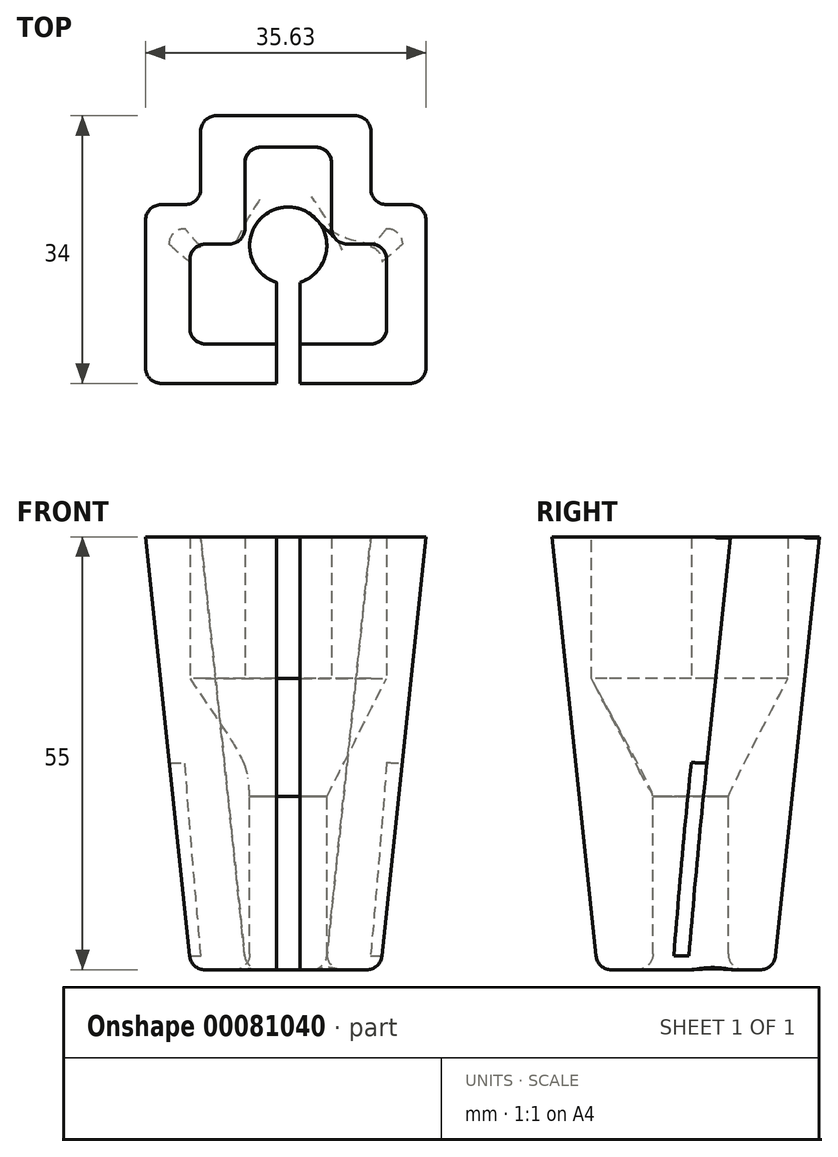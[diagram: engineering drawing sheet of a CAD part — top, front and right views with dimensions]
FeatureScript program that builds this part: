
annotation { "Feature Type Name" : "Feature", "Feature Type Description" : "" }
export const myFeature = defineFeature(function(context is Context, id is Id, definition is map)
    precondition{}
    {
        {
            var Q0;
            Q0=qCreatedBy(makeId("Top.planeOp"),FACE);
            var sketch = newSketch(context, id + "F0", { "sketchPlane" : qUnion([Q0])});
            skPoint(sketch, "E0.middle", {"position": v(0, 0) * mm});
            skLineSegment(sketch, "E1.bottom", {"start": v(10.5, -12.5) * mm, "end": v(-10.5, -12.5) * mm});
            skLineSegment(sketch, "E1.top", {"start": v(3.5, 12.5) * mm, "end": v(-3.5, 12.5) * mm});
            skLineSegment(sketch, "E1.left", {"start": v(12.5, -10.5) * mm, "end": v(12.5, -1.8) * mm});
            skLineSegment(sketch, "E1.right", {"start": v(-12.5, -10.5) * mm, "end": v(-12.5, -1.8) * mm});
            skLineSegment(sketch, "E2.top", {"start": v(-10.5, 0.2) * mm, "end": v(-7.5, 0.2) * mm});
            skLineSegment(sketch, "E2.right", {"start": v(-5.5, 10.5) * mm, "end": v(-5.5, 2.2) * mm});
            skLineSegment(sketch, "E3.top", {"start": v(10.5, 0.2) * mm, "end": v(7.5, 0.2) * mm});
            skLineSegment(sketch, "E3.right", {"start": v(5.5, 10.5) * mm, "end": v(5.5, 2.2) * mm});
            skPoint(sketch, "E4.newPointA", {"position": v(-5.5, 12.5) * mm});
            skPoint(sketch, "E4.newPointB", {"position": v(-12.5, 12.5) * mm});
            skArc(sketch, "E4.filletArc", {"start": v(-3.5, 12.5) * mm, "mid": v(-4.91, 11.91) * mm, "end": v(-5.5, 10.5) * mm});
            skArc(sketch, "E5.filletArc", {"start": v(5.5, 10.5) * mm, "mid": v(4.91, 11.91) * mm, "end": v(3.5, 12.5) * mm});
            skPoint(sketch, "E6.visualSharp", {"position": v(-5.5, 0.2) * mm});
            skArc(sketch, "E6.filletArc", {"start": v(-7.5, 0.2) * mm, "mid": v(-6.09, 0.79) * mm, "end": v(-5.5, 2.2) * mm});
            skPoint(sketch, "E7.visualSharp", {"position": v(5.5, 0.2) * mm});
            skArc(sketch, "E7.filletArc", {"start": v(5.5, 2.2) * mm, "mid": v(6.09, 0.79) * mm, "end": v(7.5, 0.2) * mm});
            skPoint(sketch, "E8.newPointA", {"position": v(-12.5, 0.2) * mm});
            skArc(sketch, "E8.filletArc", {"start": v(-10.5, 0.2) * mm, "mid": v(-11.91, -0.39) * mm, "end": v(-12.5, -1.8) * mm});
            skArc(sketch, "E9.filletArc", {"start": v(12.5, -1.8) * mm, "mid": v(11.91, -0.39) * mm, "end": v(10.5, 0.2) * mm});
            skArc(sketch, "E10.filletArc", {"start": v(15, 1.56) * mm, "mid": v(14.95, 1.99) * mm, "end": v(14.82, 2.4) * mm});
            skPoint(sketch, "E11.newPointA", {"position": v(-15, 2) * mm});
            skArc(sketch, "E11.filletArc", {"start": v(-14.82, 2.4) * mm, "mid": v(-14.95, 1.99) * mm, "end": v(-15, 1.56) * mm});
            skPoint(sketch, "E12.visualSharp", {"position": v(-12.5, -12.5) * mm});
            skArc(sketch, "E12.filletArc", {"start": v(-12.5, -10.5) * mm, "mid": v(-11.91, -11.91) * mm, "end": v(-10.5, -12.5) * mm});
            skPoint(sketch, "E13.visualSharp", {"position": v(12.5, -12.5) * mm});
            skArc(sketch, "E13.filletArc", {"start": v(10.5, -12.5) * mm, "mid": v(11.91, -11.91) * mm, "end": v(12.5, -10.5) * mm});
            skSolve(sketch);
        }
        {
            var Q0;
            Q0 = qSketchRegion(id + "F0", true);
            extrude(context, id + "F1", {"entities" : qUnion([Q0]), "depth" : 18 * mm});
        }
        {
            var Q0;
            Q0=makeQuery(id+"F1.opExtrude","CAP_FACE",FACE,{"disambiguationData":[OSD([sQuery(id+"F0.wireOp",EDGE,"E1.bottom"),sQuery(id+"F0.wireOp",EDGE,"E1.top"),sQuery(id+"F0.wireOp",EDGE,"E1.left"),sQuery(id+"F0.wireOp",EDGE,"E1.right"),sQuery(id+"F0.wireOp",EDGE,"E2.top"),sQuery(id+"F0.wireOp",EDGE,"E2.right"),sQuery(id+"F0.wireOp",EDGE,"E3.top"),sQuery(id+"F0.wireOp",EDGE,"E3.right"),sQuery(id+"F0.wireOp",EDGE,"E4.filletArc"),sQuery(id+"F0.wireOp",EDGE,"E5.filletArc"),sQuery(id+"F0.wireOp",EDGE,"E6.filletArc"),sQuery(id+"F0.wireOp",EDGE,"E7.filletArc"),sQuery(id+"F0.wireOp",EDGE,"E8.filletArc"),sQuery(id+"F0.wireOp",EDGE,"E9.filletArc"),sQuery(id+"F0.wireOp",EDGE,"E12.filletArc"),sQuery(id+"F0.wireOp",EDGE,"E13.filletArc")])],"isStart":true});
            cPlane(context, id + "F2", {"entities" : qUnion([Q0]), "cplaneType" : CPlaneType.OFFSET, "offset" : 15 * mm, "width" : 150 * mm, "height" : 150 * mm});
        }
        {
            var Q0;
            Q0=qCreatedBy(id+"F2.planeOp",FACE);
            var sketch = newSketch(context, id + "F3", { "sketchPlane" : qUnion([Q0])});
            skCircle(sketch, "E14", {"center": v(0, 0) * mm, "radius": 4.9 * mm});
            skSolve(sketch);
        }
        {
            var Q0;
            Q0 = qSketchRegion(id + "F3", true);
            extrude(context, id + "F4", {"entities" : qUnion([Q0]), "depth" : 30.48 * mm});
        }
        {
            var Q0;
            Q0=makeQuery(id+"F1.opExtrude","CAP_FACE",FACE,{"disambiguationData":[OSD([sQuery(id+"F0.wireOp",EDGE,"E1.bottom"),sQuery(id+"F0.wireOp",EDGE,"E1.top"),sQuery(id+"F0.wireOp",EDGE,"E1.left"),sQuery(id+"F0.wireOp",EDGE,"E1.right"),sQuery(id+"F0.wireOp",EDGE,"E2.top"),sQuery(id+"F0.wireOp",EDGE,"E2.right"),sQuery(id+"F0.wireOp",EDGE,"E3.top"),sQuery(id+"F0.wireOp",EDGE,"E3.right"),sQuery(id+"F0.wireOp",EDGE,"E4.filletArc"),sQuery(id+"F0.wireOp",EDGE,"E5.filletArc"),sQuery(id+"F0.wireOp",EDGE,"E6.filletArc"),sQuery(id+"F0.wireOp",EDGE,"E7.filletArc"),sQuery(id+"F0.wireOp",EDGE,"E8.filletArc"),sQuery(id+"F0.wireOp",EDGE,"E9.filletArc"),sQuery(id+"F0.wireOp",EDGE,"E12.filletArc"),sQuery(id+"F0.wireOp",EDGE,"E13.filletArc")])],"isStart":true});
            var Q1;
            Q1=makeQuery(id+"F4.opExtrude","CAP_FACE",FACE,{"disambiguationData":[OSD([sQuery(id+"F3.wireOp",EDGE,"E14")])],"isStart":true});
            loft(context, id + "F5", {"sheetProfilesArray" : [{ "sheetProfileEntities" : qUnion([Q0]) }, { "sheetProfileEntities" : qUnion([Q1]) }]});
        }
        {
            var Q0;
            Q0=makeQuery(id+"F1.opExtrude","CAP_FACE",FACE,{"disambiguationData":[OSD([sQuery(id+"F0.wireOp",EDGE,"E1.bottom"),sQuery(id+"F0.wireOp",EDGE,"E1.top"),sQuery(id+"F0.wireOp",EDGE,"E1.left"),sQuery(id+"F0.wireOp",EDGE,"E1.right"),sQuery(id+"F0.wireOp",EDGE,"E2.top"),sQuery(id+"F0.wireOp",EDGE,"E2.right"),sQuery(id+"F0.wireOp",EDGE,"E3.top"),sQuery(id+"F0.wireOp",EDGE,"E3.right"),sQuery(id+"F0.wireOp",EDGE,"E4.filletArc"),sQuery(id+"F0.wireOp",EDGE,"E5.filletArc"),sQuery(id+"F0.wireOp",EDGE,"E6.filletArc"),sQuery(id+"F0.wireOp",EDGE,"E7.filletArc"),sQuery(id+"F0.wireOp",EDGE,"E8.filletArc"),sQuery(id+"F0.wireOp",EDGE,"E9.filletArc"),sQuery(id+"F0.wireOp",EDGE,"E12.filletArc"),sQuery(id+"F0.wireOp",EDGE,"E13.filletArc")])],"isStart":false});
            var sketch = newSketch(context, id + "F6", { "sketchPlane" : qUnion([Q0])});
            skLineSegment(sketch, "E15.bottom", {"start": v(-9.13, 16.5) * mm, "end": v(8.5, 16.5) * mm});
            skLineSegment(sketch, "E15.top", {"start": v(-18.13, -17.5) * mm, "end": v(17.5, -17.5) * mm});
            skLineSegment(sketch, "E15.left", {"start": v(-18.13, 3.2) * mm, "end": v(-18.13, -17.5) * mm});
            skLineSegment(sketch, "E15.right", {"start": v(17.5, 3.2) * mm, "end": v(17.5, -17.5) * mm});
            skPoint(sketch, "E15.middle", {"position": v(0, -0.5) * mm});
            skLineSegment(sketch, "E16.bottom", {"start": v(17.5, 15.33) * mm, "end": v(10.5, 15.33) * mm});
            skLineSegment(sketch, "E16.top", {"start": v(15.5, 5.2) * mm, "end": v(12.5, 5.2) * mm});
            skLineSegment(sketch, "E16.left", {"start": v(17.5, 15.33) * mm, "end": v(17.5, 5.2) * mm});
            skLineSegment(sketch, "E16.right", {"start": v(10.5, 14.5) * mm, "end": v(10.5, 7.2) * mm});
            skLineSegment(sketch, "E17.bottom", {"start": v(-17.5, 15.33) * mm, "end": v(-10.5, 15.33) * mm});
            skLineSegment(sketch, "E17.top", {"start": v(-16.13, 5.2) * mm, "end": v(-13.13, 5.2) * mm});
            skLineSegment(sketch, "E17.left", {"start": v(-17.5, 15.33) * mm, "end": v(-17.5, 5.2) * mm});
            skLineSegment(sketch, "E17.right", {"start": v(-11.13, 14.5) * mm, "end": v(-11.13, 7.2) * mm});
            skPoint(sketch, "E18.visualSharp", {"position": v(10.5, 5.2) * mm});
            skArc(sketch, "E18.filletArc", {"start": v(10.5, 7.2) * mm, "mid": v(11.09, 5.79) * mm, "end": v(12.5, 5.2) * mm});
            skPoint(sketch, "E19.visualSharp", {"position": v(-11.13, 5.2) * mm});
            skArc(sketch, "E19.filletArc", {"start": v(-13.13, 5.2) * mm, "mid": v(-11.71, 5.79) * mm, "end": v(-11.13, 7.2) * mm});
            skPoint(sketch, "E20.newPointA", {"position": v(-17.5, 16.5) * mm});
            skArc(sketch, "E20.filletArc", {"start": v(-9.13, 16.5) * mm, "mid": v(-10.54, 15.91) * mm, "end": v(-11.13, 14.5) * mm});
            skPoint(sketch, "E21.newPointB", {"position": v(18.13, 16.5) * mm});
            skArc(sketch, "E21.filletArc", {"start": v(10.5, 14.5) * mm, "mid": v(9.91, 15.91) * mm, "end": v(8.5, 16.5) * mm});
            skArc(sketch, "E22.filletArc", {"start": v(17.5, 3.2) * mm, "mid": v(16.91, 4.61) * mm, "end": v(15.5, 5.2) * mm});
            skArc(sketch, "E23.filletArc", {"start": v(-16.13, 5.2) * mm, "mid": v(-17.54, 4.61) * mm, "end": v(-18.13, 3.2) * mm});
            skSolve(sketch);
        }
        {
            var Q0;
            Q0 = qSketchRegion(id + "F6", true);
            extrude(context, id + "F7", {"entities" : qUnion([Q0]), "oppositeDirection" : true, "depth" : 55 * mm, "hasDraft" : true, "draftAngle" : 6 * degree, "draftPullDirection" : true});
        }
        {
            var Q0;
            Q0=makeQuery(id+"F4.opExtrude","SWEPT_BODY",BODY,{"disambiguationData":[OSD([sQuery(id+"F3.wireOp",EDGE,"E14")])]});
            var Q1;
            Q1=makeQuery(id+"F1.opExtrude","SWEPT_BODY",BODY,{"disambiguationData":[OSD([sQuery(id+"F0.wireOp",EDGE,"E1.bottom"),sQuery(id+"F0.wireOp",EDGE,"E1.top"),sQuery(id+"F0.wireOp",EDGE,"E1.left"),sQuery(id+"F0.wireOp",EDGE,"E1.right"),sQuery(id+"F0.wireOp",EDGE,"E2.top"),sQuery(id+"F0.wireOp",EDGE,"E2.right"),sQuery(id+"F0.wireOp",EDGE,"E3.top"),sQuery(id+"F0.wireOp",EDGE,"E3.right"),sQuery(id+"F0.wireOp",EDGE,"E4.filletArc"),sQuery(id+"F0.wireOp",EDGE,"E5.filletArc"),sQuery(id+"F0.wireOp",EDGE,"E6.filletArc"),sQuery(id+"F0.wireOp",EDGE,"E7.filletArc"),sQuery(id+"F0.wireOp",EDGE,"E8.filletArc"),sQuery(id+"F0.wireOp",EDGE,"E9.filletArc"),sQuery(id+"F0.wireOp",EDGE,"E12.filletArc"),sQuery(id+"F0.wireOp",EDGE,"E13.filletArc")])]});
            var Q2;
            Q2=makeQuery(id+"F5.opLoft","SWEPT_BODY",BODY,{"disambiguationData":[OSD([sQuery(id+"F0.wireOp",EDGE,"E1.bottom"),sQuery(id+"F0.wireOp",EDGE,"E1.top"),sQuery(id+"F0.wireOp",EDGE,"E1.left"),sQuery(id+"F0.wireOp",EDGE,"E1.right"),sQuery(id+"F0.wireOp",EDGE,"E2.top"),sQuery(id+"F0.wireOp",EDGE,"E2.right"),sQuery(id+"F0.wireOp",EDGE,"E3.top"),sQuery(id+"F0.wireOp",EDGE,"E3.right"),sQuery(id+"F0.wireOp",EDGE,"E4.filletArc"),sQuery(id+"F0.wireOp",EDGE,"E5.filletArc"),sQuery(id+"F0.wireOp",EDGE,"E6.filletArc"),sQuery(id+"F0.wireOp",EDGE,"E7.filletArc"),sQuery(id+"F0.wireOp",EDGE,"E8.filletArc"),sQuery(id+"F0.wireOp",EDGE,"E9.filletArc"),sQuery(id+"F0.wireOp",EDGE,"E12.filletArc"),sQuery(id+"F0.wireOp",EDGE,"E13.filletArc"),sQuery(id+"F3.wireOp",EDGE,"E14")])]});
            var Q3;
            Q3=makeQuery(id+"F7.opExtrude","SWEPT_BODY",BODY,{"disambiguationData":[OSD([sQuery(id+"F6.wireOp",EDGE,"E15.bottom"),sQuery(id+"F6.wireOp",EDGE,"E15.top"),sQuery(id+"F6.wireOp",EDGE,"E15.left"),sQuery(id+"F6.wireOp",EDGE,"E15.right")])]});
            booleanBodies(context, id + "F8", {"operationType" : BooleanOperationType.SUBTRACTION, "tools" : qUnion([Q0, Q1, Q2]), "targets" : qUnion([Q3])});
        }
        {
            var Q0;
            Q0=makeQuery(id+"F7.opExtrude","CAP_FACE",FACE,{"disambiguationData":[OSD([sQuery(id+"F6.wireOp",EDGE,"E15.bottom"),sQuery(id+"F6.wireOp",EDGE,"E15.top"),sQuery(id+"F6.wireOp",EDGE,"E15.left"),sQuery(id+"F6.wireOp",EDGE,"E15.right")])],"isStart":false});
            var Q1;
            Q1=makeQuery(id+"F7.opExtrude","SWEPT_EDGE",EDGE,{"disambiguationData":[OSD([sQuery(id+"F6.wireOp",EDGE,"E15.top"),sQuery(id+"F6.wireOp",EDGE,"E15.right")])]});
            var Q2;
            Q2=makeQuery(id+"F7.opExtrude","SWEPT_EDGE",EDGE,{"disambiguationData":[OSD([sQuery(id+"F6.wireOp",EDGE,"E15.top"),sQuery(id+"F6.wireOp",EDGE,"E15.left")])]});
            var Q3;
            Q3=makeQuery(id+"F7.opExtrude","SWEPT_EDGE",EDGE,{"disambiguationData":[OSD([sQuery(id+"F6.wireOp",EDGE,"E15.bottom"),sQuery(id+"F6.wireOp",EDGE,"E15.left")])]});
            var Q4;
            Q4=makeQuery(id+"F7.opExtrude","SWEPT_EDGE",EDGE,{"disambiguationData":[OSD([sQuery(id+"F6.wireOp",EDGE,"E15.bottom"),sQuery(id+"F6.wireOp",EDGE,"E15.right")])]});
            fillet(context, id + "F9", {"entities" : qUnion([Q0, Q1, Q2, Q3, Q4]), "radius" : 2 * mm, "tangentPropagation" : true, "allowEdgeOverflow" : false});
        }
        {
            var Q0;
            Q0=qCreatedBy(makeId("Front.planeOp"),FACE);
            var sketch = newSketch(context, id + "F10", { "sketchPlane" : qUnion([Q0])});
            skLineSegment(sketch, "E24.bottom", {"start": v(1.5, 45) * mm, "end": v(-1.5, 45) * mm});
            skLineSegment(sketch, "E24.top", {"start": v(1.5, -45) * mm, "end": v(-1.5, -45) * mm});
            skLineSegment(sketch, "E24.left", {"start": v(1.5, 45) * mm, "end": v(1.5, -45) * mm});
            skLineSegment(sketch, "E24.right", {"start": v(-1.5, 45) * mm, "end": v(-1.5, -45) * mm});
            skPoint(sketch, "E24.middle", {"position": v(0, 0) * mm});
            skSolve(sketch);
        }
        {
            var Q0;
            Q0 = qSketchRegion(id + "F10", true);
            extrude(context, id + "F11", {"entities" : qUnion([Q0]), "operationType" : NewBodyOperationType.REMOVE, "depth" : 25 * mm});
        }
    });
